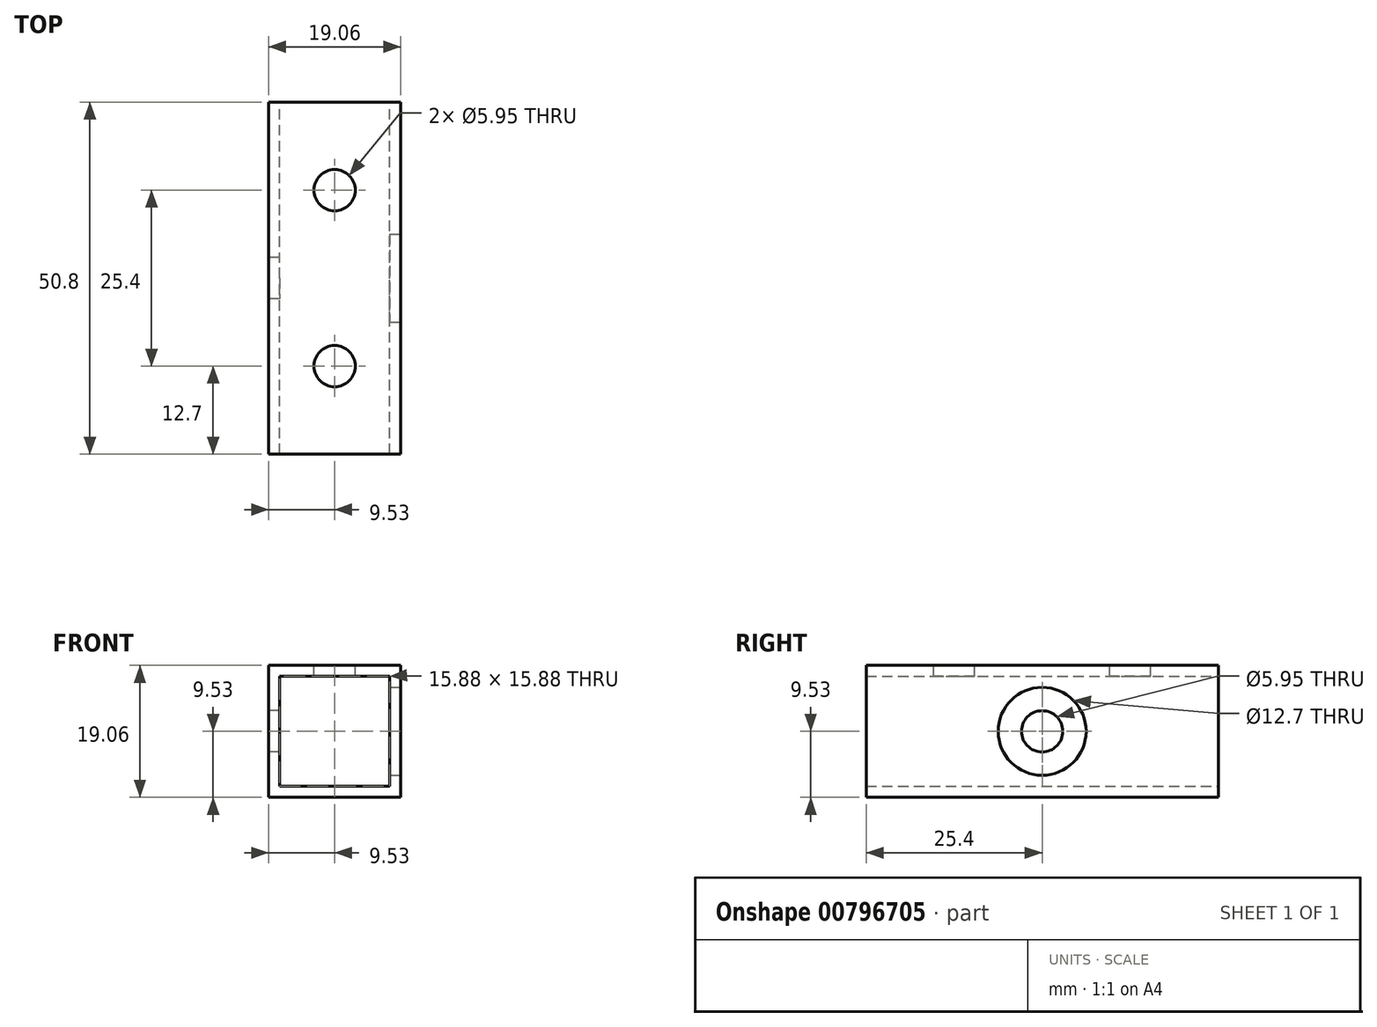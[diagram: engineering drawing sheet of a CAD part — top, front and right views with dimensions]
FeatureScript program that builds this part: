
annotation { "Feature Type Name" : "Feature", "Feature Type Description" : "" }
export const myFeature = defineFeature(function(context is Context, id is Id, definition is map)
    precondition{}
    {
        {
            var Q0;
            Q0=qCreatedBy(makeId("Front.planeOp"),FACE);
            var sketch = newSketch(context, id + "F0", { "sketchPlane" : qUnion([Q0])});
            skLineSegment(sketch, "E0.bottom", {"start": v(-9.52, 9.53) * mm, "end": v(9.53, 9.53) * mm});
            skLineSegment(sketch, "E0.top", {"start": v(-9.53, -9.53) * mm, "end": v(9.52, -9.53) * mm});
            skLineSegment(sketch, "E0.left", {"start": v(-9.52, 9.53) * mm, "end": v(-9.53, -9.52) * mm});
            skLineSegment(sketch, "E0.right", {"start": v(9.53, 9.53) * mm, "end": v(9.52, -9.52) * mm});
            skPoint(sketch, "E0.middle", {"position": v(0, 0) * mm});
            skLineSegment(sketch, "E1.bottom", {"start": v(-7.94, 7.94) * mm, "end": v(7.94, 7.94) * mm});
            skLineSegment(sketch, "E1.top", {"start": v(-7.94, -7.94) * mm, "end": v(7.94, -7.94) * mm});
            skLineSegment(sketch, "E1.left", {"start": v(-7.94, 7.94) * mm, "end": v(-7.94, -7.94) * mm});
            skLineSegment(sketch, "E1.right", {"start": v(7.94, 7.94) * mm, "end": v(7.94, -7.94) * mm});
            skSolve(sketch);
        }
        {
            var Q0;
            Q0=qSketchRegion(id+"F0",true);
            extrude(context, id + "F1", {"entities" : qUnion([Q0]), "depth" : 50.8 * mm, "offsetDistance" : 25.4 * mm});
        }
        {
            var Q0;
            Q0=makeQuery(id+"F1.opExtrude","SWEPT_FACE",FACE,{"disambiguationData":[OSD([sQuery(id+"F0.wireOp",EDGE,"E0.left")])]});
            var sketch = newSketch(context, id + "F2", { "sketchPlane" : qUnion([Q0])});
            skPoint(sketch, "E2", {"position": v(25.4, 0) * mm});
            skSolve(sketch);
        }
        {
            var Q0;
            Q0=sQuery(id+"F2.wireOp",VERTEX,"E2");
            var Q1;
            Q1=makeQuery(id+"F1.opExtrude","SWEPT_BODY",BODY,{"disambiguationData":[OSD([sQuery(id+"F0.wireOp",EDGE,"E0.bottom"),sQuery(id+"F0.wireOp",EDGE,"E0.top"),sQuery(id+"F0.wireOp",EDGE,"E0.left"),sQuery(id+"F0.wireOp",EDGE,"E0.right"),sQuery(id+"F0.wireOp",EDGE,"E1.bottom"),sQuery(id+"F0.wireOp",EDGE,"E1.top"),sQuery(id+"F0.wireOp",EDGE,"E1.left"),sQuery(id+"F0.wireOp",EDGE,"E1.right")])]});
            hole(context, id + "F3", {"style" : HoleStyle.SIMPLE, "endStyle" : HoleEndStyle.BLIND, "holeDiameter" : 5.95 * mm, "majorDiameter" : 6.35 * mm, "holeDepth" : 6.35 * mm, "isTappedThrough" : true, "tappedDepth" : 12.7 * mm, "tapClearance" : 3, "startFromSketch" : true, "locations" : qUnion([Q0]), "scope" : qUnion([Q1])});
        }
        {
            var Q0;
            Q0=makeQuery(id+"F1.opExtrude","SWEPT_FACE",FACE,{"disambiguationData":[OSD([sQuery(id+"F0.wireOp",EDGE,"E0.right")])]});
            var sketch = newSketch(context, id + "F4", { "sketchPlane" : qUnion([Q0])});
            skPoint(sketch, "E3", {"position": v(-25.4, 0) * mm});
            skSolve(sketch);
        }
        {
            var Q0;
            Q0=sQuery(id+"F4.wireOp",VERTEX,"E3");
            var Q1;
            Q1=makeQuery(id+"F1.opExtrude","SWEPT_BODY",BODY,{"disambiguationData":[OSD([sQuery(id+"F0.wireOp",EDGE,"E0.bottom"),sQuery(id+"F0.wireOp",EDGE,"E0.top"),sQuery(id+"F0.wireOp",EDGE,"E0.left"),sQuery(id+"F0.wireOp",EDGE,"E0.right"),sQuery(id+"F0.wireOp",EDGE,"E1.bottom"),sQuery(id+"F0.wireOp",EDGE,"E1.top"),sQuery(id+"F0.wireOp",EDGE,"E1.left"),sQuery(id+"F0.wireOp",EDGE,"E1.right")])]});
            hole(context, id + "F5", {"style" : HoleStyle.SIMPLE, "endStyle" : HoleEndStyle.BLIND, "holeDiameter" : 12.7 * mm, "majorDiameter" : 6.35 * mm, "holeDepth" : 6.35 * mm, "isTappedThrough" : true, "tappedDepth" : 12.7 * mm, "tapClearance" : 3, "startFromSketch" : true, "locations" : qUnion([Q0]), "scope" : qUnion([Q1])});
        }
        {
            var Q0;
            Q0=makeQuery(id+"F1.opExtrude","SWEPT_FACE",FACE,{"disambiguationData":[OSD([sQuery(id+"F0.wireOp",EDGE,"E0.bottom")])]});
            var sketch = newSketch(context, id + "F6", { "sketchPlane" : qUnion([Q0])});
            skPoint(sketch, "E4", {"position": v(0, -12.7) * mm});
            skPoint(sketch, "E5", {"position": v(0, -38.1) * mm});
            skSolve(sketch);
        }
        {
            var Q0;
            Q0=sQuery(id+"F6.wireOp",VERTEX,"E4");
            var Q1;
            Q1=sQuery(id+"F6.wireOp",VERTEX,"E5");
            var Q2;
            Q2=makeQuery(id+"F1.opExtrude","SWEPT_BODY",BODY,{"disambiguationData":[OSD([sQuery(id+"F0.wireOp",EDGE,"E0.bottom"),sQuery(id+"F0.wireOp",EDGE,"E0.top"),sQuery(id+"F0.wireOp",EDGE,"E0.left"),sQuery(id+"F0.wireOp",EDGE,"E0.right"),sQuery(id+"F0.wireOp",EDGE,"E1.bottom"),sQuery(id+"F0.wireOp",EDGE,"E1.top"),sQuery(id+"F0.wireOp",EDGE,"E1.left"),sQuery(id+"F0.wireOp",EDGE,"E1.right")])]});
            hole(context, id + "F7", {"style" : HoleStyle.SIMPLE, "endStyle" : HoleEndStyle.BLIND, "holeDiameter" : 5.95 * mm, "majorDiameter" : 6.35 * mm, "holeDepth" : 6.35 * mm, "isTappedThrough" : true, "tappedDepth" : 12.7 * mm, "tapClearance" : 3, "startFromSketch" : true, "locations" : qUnion([Q0, Q1]), "scope" : qUnion([Q2])});
        }
    });
